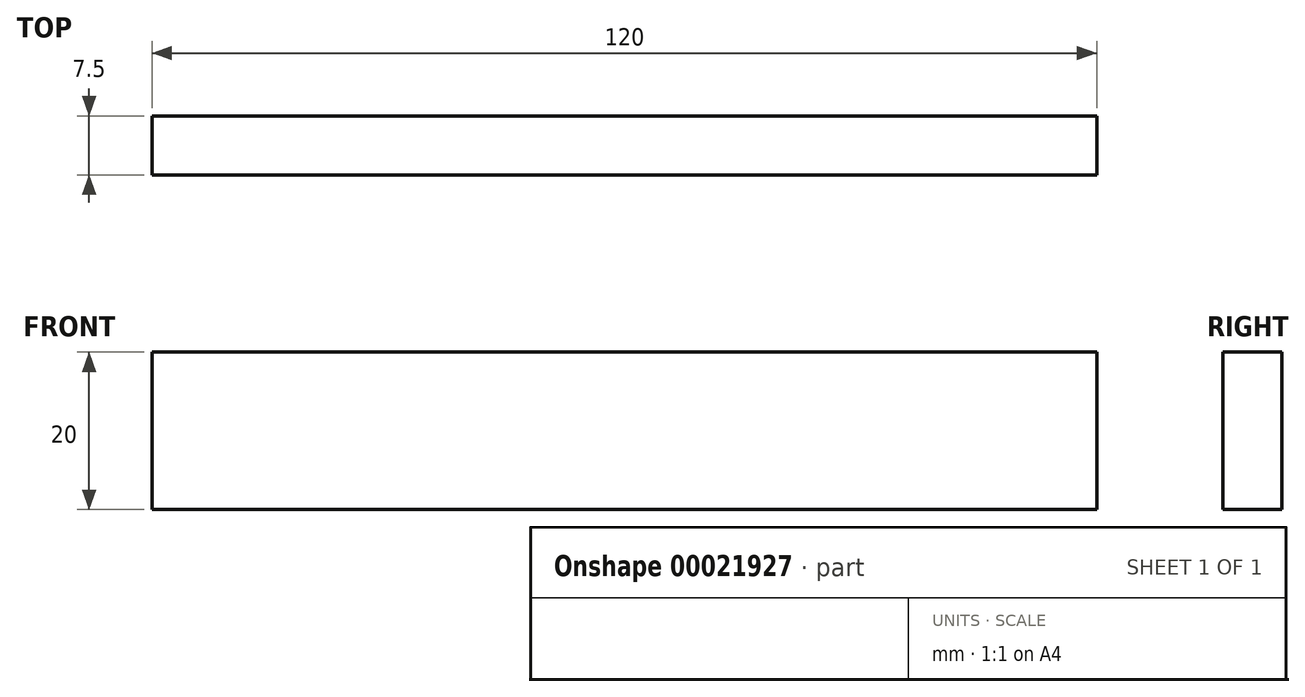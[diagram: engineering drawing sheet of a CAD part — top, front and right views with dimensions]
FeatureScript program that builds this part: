
annotation { "Feature Type Name" : "Feature", "Feature Type Description" : "" }
export const myFeature = defineFeature(function(context is Context, id is Id, definition is map)
    precondition{}
    {
        {
            var Q0;
            Q0=qCreatedBy(makeId("Front.planeOp"),FACE);
            var sketch = newSketch(context, id + "F0", { "sketchPlane" : qUnion([Q0])});
            skLineSegment(sketch, "E0.rect.bottom", {"start": v(60, 10) * mm, "end": v(-60, 10) * mm});
            skLineSegment(sketch, "E0.rect.top", {"start": v(60, -10) * mm, "end": v(-60, -10) * mm});
            skLineSegment(sketch, "E0.rect.left", {"start": v(60, 10) * mm, "end": v(60, -10) * mm});
            skLineSegment(sketch, "E0.rect.right", {"start": v(-60, 10) * mm, "end": v(-60, -10) * mm});
            skPoint(sketch, "E0.rect.middle", {"position": v(0, 0) * mm});
            skSolve(sketch);
        }
        {
            var Q0;
            Q0=makeQuery(id+"F0.imprint","IMPRINT",FACE,{"disambiguationData":[TD([[makeQuery(id+"F0.imprint","IMPRINT",EDGE,{"derivedFrom":sQuery(id+"F0.wireOp",EDGE,"E0.rect.bottom")}),1.0]])]});
            extrude(context, id + "F1", {"entities" : qUnion([Q0]), "depth" : 7.5 * mm});
        }
    });
